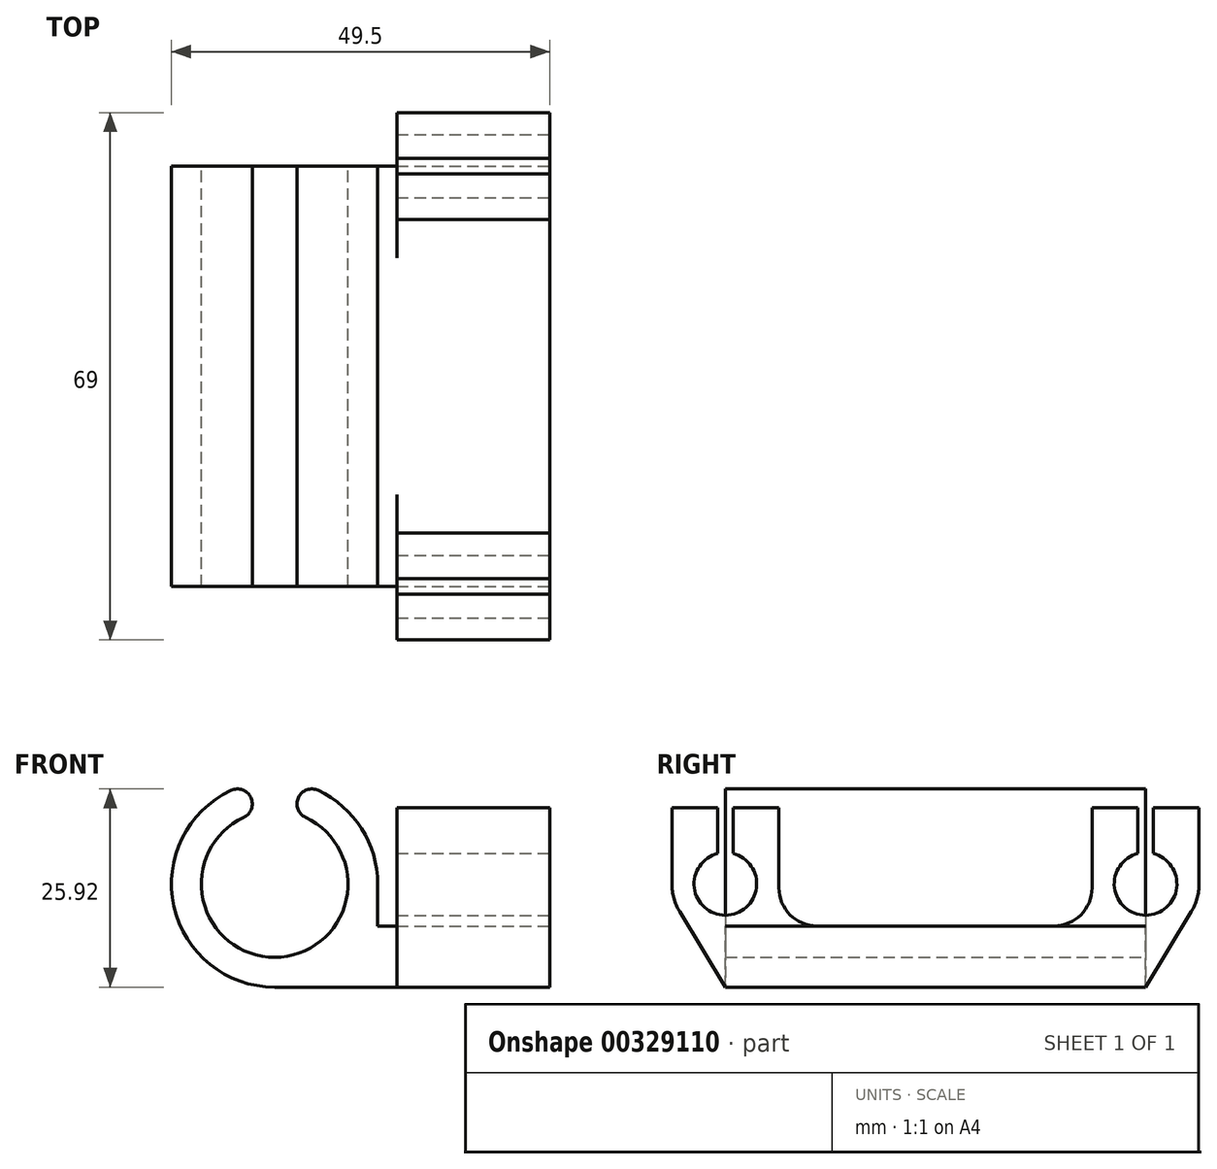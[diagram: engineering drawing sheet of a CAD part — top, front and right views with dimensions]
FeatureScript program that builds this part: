
annotation { "Feature Type Name" : "Feature", "Feature Type Description" : "" }
export const myFeature = defineFeature(function(context is Context, id is Id, definition is map)
    precondition{}
    {
        {
            var Q0;
            Q0=qCreatedBy(makeId("Front.planeOp"),FACE);
            var sketch = newSketch(context, id + "F0", { "sketchPlane" : qUnion([Q0])});
            skArc(sketch, "E0", {"start": v(-4.06, 8.7) * mm, "mid": v(0, -9.6) * mm, "end": v(4.06, 8.7) * mm});
            skArc(sketch, "E1", {"start": v(13.5, 0) * mm, "mid": v(11.39, 7.25) * mm, "end": v(5.7, 12.24) * mm});
            skLineSegment(sketch, "E2", {"start": v(0, -13.5) * mm, "end": v(36, -13.5) * mm});
            skLineSegment(sketch, "E3", {"start": v(36, -13.5) * mm, "end": v(36, -5.5) * mm});
            skLineSegment(sketch, "E4", {"start": v(36, -5.5) * mm, "end": v(13.5, -5.5) * mm});
            skLineSegment(sketch, "E5", {"start": v(13.5, 0) * mm, "end": v(13.5, -5.5) * mm});
            skLineSegment(sketch, "E6", {"start": v(0, 0) * mm, "end": v(0, 13.5) * mm, "construction": true});
            skLineSegment(sketch, "E7", {"start": v(0, 0) * mm, "end": v(-5.7, 12.24) * mm, "construction": true});
            skLineSegment(sketch, "E8", {"start": v(0, 0) * mm, "end": v(5.7, 12.24) * mm, "construction": true});
            skArc(sketch, "E9.trimOffspring", {"start": v(-5.7, 12.24) * mm, "mid": v(-13.18, -2.92) * mm, "end": v(0, -13.5) * mm});
            skArc(sketch, "E10", {"start": v(5.7, 12.24) * mm, "mid": v(3.11, 11.3) * mm, "end": v(4.06, 8.7) * mm});
            skArc(sketch, "E11", {"start": v(-4.06, 8.7) * mm, "mid": v(-3.11, 11.3) * mm, "end": v(-5.7, 12.24) * mm});
            skSolve(sketch);
        }
        {
            var Q0;
            Q0 = qSketchRegion(id + "F0", true);
            extrude(context, id + "F1", {"entities" : qUnion([Q0]), "endBound" : BoundingType.SYMMETRIC, "depth" : 55 * mm});
        }
        {
            var Q0;
            Q0=makeQuery(id+"F1.opExtrude","SWEPT_FACE",FACE,{"disambiguationData":[OSD([sQuery(id+"F0.wireOp",EDGE,"E3")])]});
            var sketch = newSketch(context, id + "F2", { "sketchPlane" : qUnion([Q0])});
            skLineSegment(sketch, "E12", {"start": v(0, 0) * mm, "end": v(-27.5, 0) * mm, "construction": true});
            skArc(sketch, "E13", {"start": v(-28.5, 3.98) * mm, "mid": v(-27.5, -4.1) * mm, "end": v(-26.5, 3.98) * mm});
            skArc(sketch, "E14", {"start": v(-34.5, 0) * mm, "mid": v(-34.24, -1.88) * mm, "end": v(-33.49, -3.63) * mm});
            skLineSegment(sketch, "E15", {"start": v(-27.5, -13.5) * mm, "end": v(-33.49, -3.63) * mm});
            skLineSegment(sketch, "E16", {"start": v(-20.5, 0) * mm, "end": v(-20.5, -0.5) * mm});
            skLineSegment(sketch, "E17", {"start": v(-27.5, -13.5) * mm, "end": v(0, -13.5) * mm});
            skLineSegment(sketch, "E18", {"start": v(-15.5, -5.5) * mm, "end": v(0, -5.5) * mm});
            skPoint(sketch, "E19.visualSharp", {"position": v(-20.5, -5.5) * mm});
            skArc(sketch, "E19.filletArc", {"start": v(-20.5, -0.5) * mm, "mid": v(-19.04, -4.04) * mm, "end": v(-15.5, -5.5) * mm});
            skLineSegment(sketch, "E20", {"start": v(-27.5, 0) * mm, "end": v(-27.5, 10) * mm, "construction": true});
            skLineSegment(sketch, "E21.0", {"start": v(-26.5, 3.98) * mm, "end": v(-26.5, 10) * mm});
            skLineSegment(sketch, "E22.0", {"start": v(-20.5, 0) * mm, "end": v(-20.5, 10) * mm});
            skLineSegment(sketch, "E23.0", {"start": v(-28.5, 3.98) * mm, "end": v(-28.5, 10) * mm});
            skLineSegment(sketch, "E24.0", {"start": v(-34.5, 0) * mm, "end": v(-34.5, 10) * mm});
            skLineSegment(sketch, "E25", {"start": v(-34.5, 10) * mm, "end": v(-28.5, 10) * mm});
            skLineSegment(sketch, "E26", {"start": v(-27.5, 10) * mm, "end": v(-28.5, 10) * mm, "construction": true});
            skLineSegment(sketch, "E27", {"start": v(-27.5, 10) * mm, "end": v(-26.5, 10) * mm, "construction": true});
            skLineSegment(sketch, "E28", {"start": v(-26.5, 10) * mm, "end": v(-20.5, 10) * mm});
            skLineSegment(sketch, "E29", {"start": v(0, 0) * mm, "end": v(0, -5.5) * mm, "construction": true});
            skLineSegment(sketch, "E30.MirrorCS", {"start": v(15.5, -5.5) * mm, "end": v(0, -5.5) * mm});
            skArc(sketch, "E31.MirrorCS", {"start": v(20.5, -0.5) * mm, "mid": v(19.04, -4.04) * mm, "end": v(15.5, -5.5) * mm});
            skLineSegment(sketch, "E32.MirrorCS", {"start": v(20.5, 0) * mm, "end": v(20.5, -0.5) * mm});
            skLineSegment(sketch, "E33.MirrorCS", {"start": v(20.5, 0) * mm, "end": v(20.5, 10) * mm});
            skLineSegment(sketch, "E34.MirrorCS", {"start": v(26.5, 10) * mm, "end": v(20.5, 10) * mm});
            skLineSegment(sketch, "E35.MirrorCS", {"start": v(26.5, 3.98) * mm, "end": v(26.5, 10) * mm});
            skArc(sketch, "E36.MirrorCS", {"start": v(28.5, 3.98) * mm, "mid": v(27.5, -4.1) * mm, "end": v(26.5, 3.98) * mm});
            skLineSegment(sketch, "E37.MirrorCS", {"start": v(28.5, 3.98) * mm, "end": v(28.5, 10) * mm});
            skLineSegment(sketch, "E38.MirrorCS", {"start": v(34.5, 10) * mm, "end": v(28.5, 10) * mm});
            skLineSegment(sketch, "E39.MirrorCS", {"start": v(34.5, 0) * mm, "end": v(34.5, 10) * mm});
            skArc(sketch, "E40.MirrorCS", {"start": v(34.5, 0) * mm, "mid": v(34.24, -1.88) * mm, "end": v(33.49, -3.63) * mm});
            skLineSegment(sketch, "E41.MirrorCS", {"start": v(27.5, -13.5) * mm, "end": v(33.49, -3.63) * mm});
            skLineSegment(sketch, "E42.MirrorCS", {"start": v(27.5, -13.5) * mm, "end": v(0, -13.5) * mm});
            skSolve(sketch);
        }
        {
            var Q0;
            Q0 = qSketchRegion(id + "F2", true);
            extrude(context, id + "F3", {"entities" : qUnion([Q0]), "operationType" : NewBodyOperationType.ADD, "oppositeDirection" : true, "depth" : 20 * mm});
        }
    });
